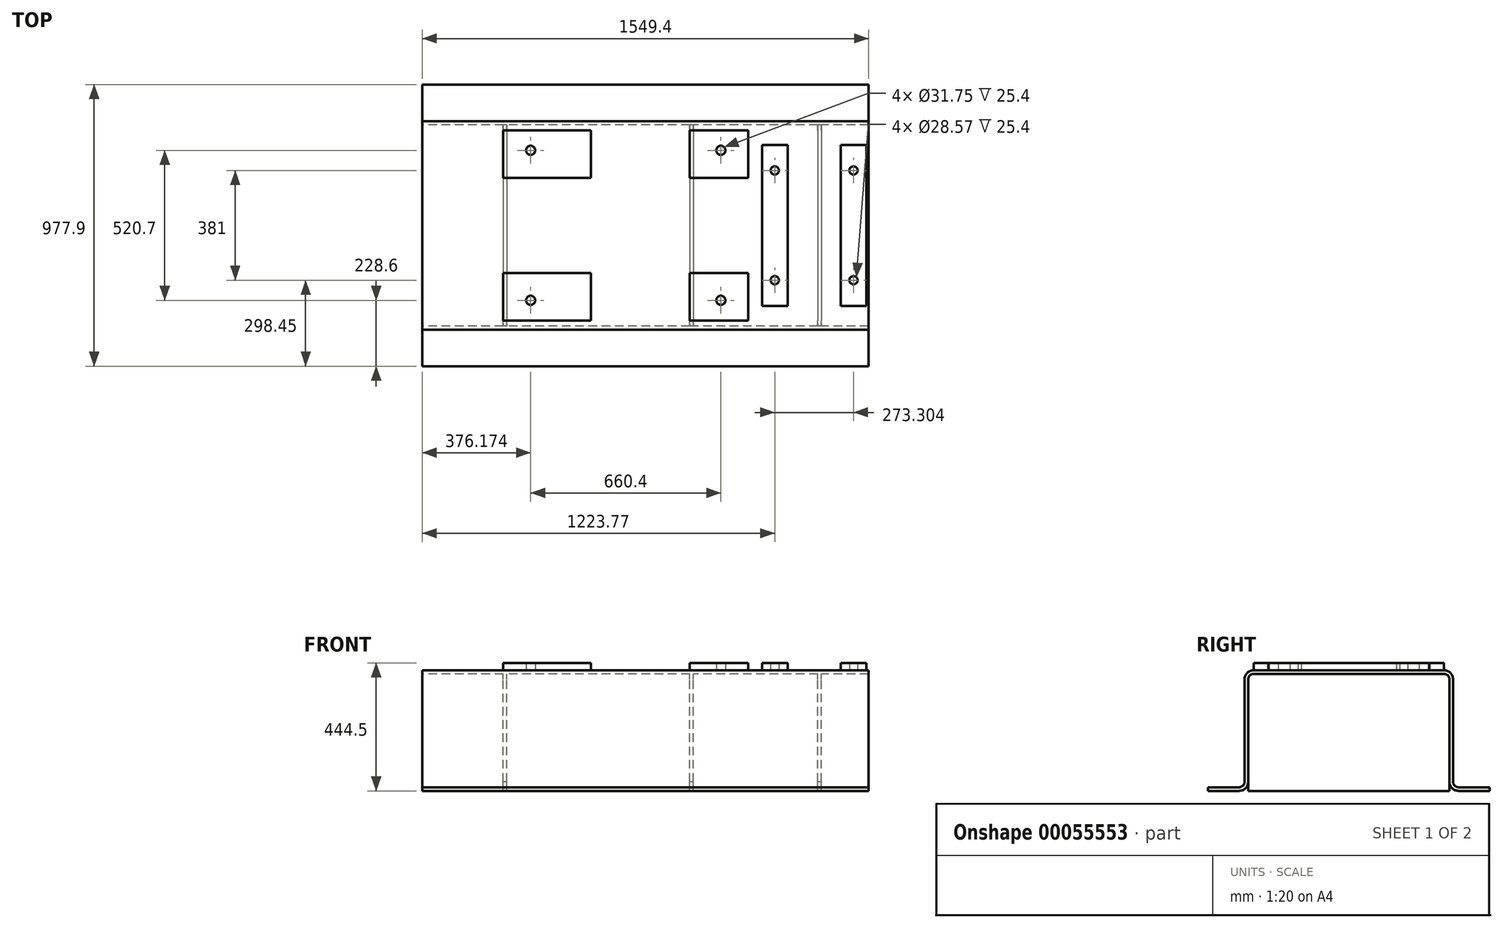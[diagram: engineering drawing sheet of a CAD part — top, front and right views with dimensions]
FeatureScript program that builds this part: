
annotation { "Feature Type Name" : "Feature", "Feature Type Description" : "" }
export const myFeature = defineFeature(function(context is Context, id is Id, definition is map)
    precondition{}
    {
        {
            var Q0;
            Q0=qCreatedBy(makeId("Right.planeOp"),FACE);
            var sketch = newSketch(context, id + "F0", { "sketchPlane" : qUnion([Q0])});
            skLineSegment(sketch, "E0", {"start": v(-488.95, 0) * mm, "end": v(488.95, 0) * mm, "construction": true});
            skLineSegment(sketch, "E1.0", {"start": v(-488.95, 419.1) * mm, "end": v(488.95, 419.1) * mm, "construction": true});
            skLineSegment(sketch, "E2", {"start": v(0, 0) * mm, "end": v(0, 550.43) * mm, "construction": true});
            skLineSegment(sketch, "E3.0", {"start": v(-361.95, 0) * mm, "end": v(-361.95, 550.43) * mm, "construction": true});
            skLineSegment(sketch, "E4.0", {"start": v(-488.95, 12.7) * mm, "end": v(488.95, 12.7) * mm, "construction": true});
            skLineSegment(sketch, "E5.0", {"start": v(-349.25, 0) * mm, "end": v(-349.25, 550.43) * mm, "construction": true});
            skLineSegment(sketch, "E6.0", {"start": v(-488.95, 406.4) * mm, "end": v(488.95, 406.4) * mm, "construction": true});
            skLineSegment(sketch, "E7", {"start": v(-488.95, 0) * mm, "end": v(-381, 0) * mm});
            skLineSegment(sketch, "E8", {"start": v(-349.25, 31.75) * mm, "end": v(-349.25, 387.35) * mm});
            skLineSegment(sketch, "E9", {"start": v(-330.2, 406.4) * mm, "end": v(0, 406.4) * mm});
            skLineSegment(sketch, "E10", {"start": v(0, 406.4) * mm, "end": v(0, 419.1) * mm});
            skLineSegment(sketch, "E11", {"start": v(0, 419.1) * mm, "end": v(-330.2, 419.1) * mm});
            skLineSegment(sketch, "E12", {"start": v(-361.95, 387.35) * mm, "end": v(-361.95, 31.75) * mm});
            skLineSegment(sketch, "E13", {"start": v(-381, 12.7) * mm, "end": v(-488.95, 12.7) * mm});
            skLineSegment(sketch, "E14", {"start": v(-488.95, 12.7) * mm, "end": v(-488.95, 0) * mm});
            skPoint(sketch, "E15.visualSharp", {"position": v(-349.25, 406.4) * mm});
            skArc(sketch, "E15.filletArc", {"start": v(-330.2, 406.4) * mm, "mid": v(-343.67, 400.82) * mm, "end": v(-349.25, 387.35) * mm});
            skPoint(sketch, "E16.visualSharp", {"position": v(-361.95, 12.7) * mm});
            skArc(sketch, "E16.filletArc", {"start": v(-381, 12.7) * mm, "mid": v(-367.53, 18.28) * mm, "end": v(-361.95, 31.75) * mm});
            skPoint(sketch, "E17.visualSharp", {"position": v(-349.25, 0) * mm});
            skArc(sketch, "E17.filletArc", {"start": v(-381, 0) * mm, "mid": v(-358.55, 9.3) * mm, "end": v(-349.25, 31.75) * mm});
            skPoint(sketch, "E18.visualSharp", {"position": v(-361.95, 419.1) * mm});
            skArc(sketch, "E18.filletArc", {"start": v(-330.2, 419.1) * mm, "mid": v(-352.65, 409.8) * mm, "end": v(-361.95, 387.35) * mm});
            skArc(sketch, "E19.MirrorCS", {"start": v(381, 12.7) * mm, "mid": v(367.53, 18.28) * mm, "end": v(361.95, 31.75) * mm});
            skLineSegment(sketch, "E20.MirrorCS", {"start": v(488.95, 12.7) * mm, "end": v(488.95, 0) * mm});
            skArc(sketch, "E21.MirrorCS", {"start": v(330.2, 406.4) * mm, "mid": v(343.67, 400.82) * mm, "end": v(349.25, 387.35) * mm});
            skArc(sketch, "E22.MirrorCS", {"start": v(381, 0) * mm, "mid": v(358.55, 9.3) * mm, "end": v(349.25, 31.75) * mm});
            skArc(sketch, "E23.MirrorCS", {"start": v(330.2, 419.1) * mm, "mid": v(352.65, 409.8) * mm, "end": v(361.95, 387.35) * mm});
            skPoint(sketch, "E24.MirrorP", {"position": v(361.95, 419.1) * mm});
            skLineSegment(sketch, "E25.MirrorCS", {"start": v(488.95, 0) * mm, "end": v(381, 0) * mm});
            skPoint(sketch, "E26.MirrorP", {"position": v(349.25, 0) * mm});
            skLineSegment(sketch, "E27.MirrorCS", {"start": v(330.2, 406.4) * mm, "end": v(0, 406.4) * mm});
            skLineSegment(sketch, "E28.MirrorCS", {"start": v(349.25, 31.75) * mm, "end": v(349.25, 387.35) * mm});
            skLineSegment(sketch, "E29.MirrorCS", {"start": v(381, 12.7) * mm, "end": v(488.95, 12.7) * mm});
            skLineSegment(sketch, "E30.MirrorCS", {"start": v(361.95, 387.35) * mm, "end": v(361.95, 31.75) * mm});
            skLineSegment(sketch, "E31.MirrorCS", {"start": v(0, 419.1) * mm, "end": v(330.2, 419.1) * mm});
            skPoint(sketch, "E32.MirrorP", {"position": v(349.25, 406.4) * mm});
            skPoint(sketch, "E33.MirrorP", {"position": v(361.95, 12.7) * mm});
            skSolve(sketch);
        }
        {
            var Q0;
            Q0 = qSketchRegion(id + "F0", true);
            extrude(context, id + "F1", {"entities" : qUnion([Q0]), "endBound" : BoundingType.SYMMETRIC, "depth" : 1549.4 * mm});
        }
        {
            var Q0;
            Q0=makeQuery(id+"F1.opExtrude","SWEPT_FACE",FACE,{"disambiguationData":[OSD([sQuery(id+"F0.wireOp",EDGE,"E11"),sQuery(id+"F0.wireOp",EDGE,"E31.MirrorCS")])]});
            var sketch = newSketch(context, id + "F2", { "sketchPlane" : qUnion([Q0])});
            skLineSegment(sketch, "E34.0", {"start": v(774.7, 330.2) * mm, "end": v(774.7, -330.2) * mm, "construction": true});
            skLineSegment(sketch, "E35.0", {"start": v(-1612.9, 330.2) * mm, "end": v(-1612.9, -330.2) * mm, "construction": true});
            skLineSegment(sketch, "E36.0", {"start": v(-1130.3, 330.2) * mm, "end": v(-1130.3, -330.2) * mm, "construction": true});
            skLineSegment(sketch, "E37.0", {"start": v(-68.33, 330.2) * mm, "end": v(-68.33, -330.2) * mm, "construction": true});
            skLineSegment(sketch, "E38.0", {"start": v(585.72, 330.2) * mm, "end": v(585.72, -330.2) * mm, "construction": true});
            skLineSegment(sketch, "E39", {"start": v(1112.44, 0) * mm, "end": v(-1758.43, 0) * mm, "construction": true});
            skLineSegment(sketch, "E40.0", {"start": v(153.92, 330.2) * mm, "end": v(153.92, -330.2) * mm, "construction": true});
            skLineSegment(sketch, "E41.0", {"start": v(357.12, 330.2) * mm, "end": v(357.12, -330.2) * mm, "construction": true});
            skLineSegment(sketch, "E42.0", {"start": v(-188.98, 330.2) * mm, "end": v(-188.98, -330.2) * mm, "construction": true});
            skLineSegment(sketch, "E43.0", {"start": v(-493.78, 330.2) * mm, "end": v(-493.78, -330.2) * mm, "construction": true});
            skLineSegment(sketch, "E44.0", {"start": v(1112.44, 165.1) * mm, "end": v(-1758.43, 165.1) * mm, "construction": true});
            skLineSegment(sketch, "E45.0", {"start": v(1112.44, 330.2) * mm, "end": v(-1758.43, 330.2) * mm, "construction": true});
            skLineSegment(sketch, "E46.bottom", {"start": v(-493.78, 330.2) * mm, "end": v(-188.98, 330.2) * mm});
            skLineSegment(sketch, "E46.top", {"start": v(-493.78, 165.1) * mm, "end": v(-188.98, 165.1) * mm});
            skLineSegment(sketch, "E46.left", {"start": v(-493.78, 330.2) * mm, "end": v(-493.78, 165.1) * mm});
            skLineSegment(sketch, "E46.right", {"start": v(-188.98, 330.2) * mm, "end": v(-188.98, 165.1) * mm});
            skLineSegment(sketch, "E47.bottom", {"start": v(153.92, 330.2) * mm, "end": v(357.12, 330.2) * mm});
            skLineSegment(sketch, "E47.top", {"start": v(153.92, 165.1) * mm, "end": v(357.12, 165.1) * mm});
            skLineSegment(sketch, "E47.left", {"start": v(153.92, 330.2) * mm, "end": v(153.92, 165.1) * mm});
            skLineSegment(sketch, "E47.right", {"start": v(357.12, 330.2) * mm, "end": v(357.12, 165.1) * mm});
            skLineSegment(sketch, "E48.0", {"start": v(-398.53, 330.2) * mm, "end": v(-398.53, -330.2) * mm, "construction": true});
            skLineSegment(sketch, "E49.0", {"start": v(261.87, 330.2) * mm, "end": v(261.87, -330.2) * mm, "construction": true});
            skLineSegment(sketch, "E50.0", {"start": v(1112.44, 260.35) * mm, "end": v(-1758.43, 260.35) * mm, "construction": true});
            skCircle(sketch, "E51", {"center": v(-398.53, 260.35) * mm, "radius": 15.88 * mm});
            skCircle(sketch, "E52", {"center": v(261.87, 260.35) * mm, "radius": 15.88 * mm});
            skLineSegment(sketch, "E53.MirrorCS", {"start": v(-493.78, -165.1) * mm, "end": v(-188.98, -165.1) * mm});
            skLineSegment(sketch, "E54.MirrorCS", {"start": v(-493.78, -330.2) * mm, "end": v(-188.98, -330.2) * mm});
            skLineSegment(sketch, "E55.MirrorCS", {"start": v(-493.78, -330.2) * mm, "end": v(-493.78, -165.1) * mm});
            skLineSegment(sketch, "E56.MirrorCS", {"start": v(-188.98, -330.2) * mm, "end": v(-188.98, -165.1) * mm});
            skLineSegment(sketch, "E57.MirrorCS", {"start": v(153.92, -330.2) * mm, "end": v(357.12, -330.2) * mm});
            skLineSegment(sketch, "E58.MirrorCS", {"start": v(153.92, -165.1) * mm, "end": v(357.12, -165.1) * mm});
            skCircle(sketch, "E59.MirrorC", {"center": v(-398.53, -260.35) * mm, "radius": 15.88 * mm});
            skLineSegment(sketch, "E60.MirrorCS", {"start": v(357.12, -330.2) * mm, "end": v(357.12, -165.1) * mm});
            skLineSegment(sketch, "E61.MirrorCS", {"start": v(153.92, -330.2) * mm, "end": v(153.92, -165.1) * mm});
            skCircle(sketch, "E62.MirrorC", {"center": v(261.87, -260.35) * mm, "radius": 15.88 * mm});
            skSolve(sketch);
        }
        {
            var Q0;
            Q0 = qSketchRegion(id + "F2", true);
            extrude(context, id + "F3", {"entities" : qUnion([Q0]), "operationType" : NewBodyOperationType.ADD, "depth" : 25.4 * mm});
        }
        {
            var Q0;
            Q0=makeQuery(id+"F1.opExtrude","SWEPT_FACE",FACE,{"disambiguationData":[OSD([sQuery(id+"F0.wireOp",EDGE,"E9"),sQuery(id+"F0.wireOp",EDGE,"E27.MirrorCS")])]});
            var sketch = newSketch(context, id + "F4", { "sketchPlane" : qUnion([Q0])});
            skLineSegment(sketch, "E63.0", {"start": v(585.72, -330.2) * mm, "end": v(585.72, 330.2) * mm, "construction": true});
            skLineSegment(sketch, "E64.0", {"start": v(1112.44, 0) * mm, "end": v(-1758.43, 0) * mm, "construction": true});
            skLineSegment(sketch, "E65.0", {"start": v(493.78, -330.2) * mm, "end": v(493.78, 330.2) * mm, "construction": true});
            skLineSegment(sketch, "E66.0", {"start": v(677.67, -330.2) * mm, "end": v(677.67, 330.2) * mm, "construction": true});
            skLineSegment(sketch, "E67.0", {"start": v(766.57, -330.2) * mm, "end": v(766.57, 330.2) * mm, "construction": true});
            skLineSegment(sketch, "E68.0", {"start": v(404.88, -330.2) * mm, "end": v(404.88, 330.2) * mm, "construction": true});
            skLineSegment(sketch, "E69.bottom", {"start": v(404.88, -279.4) * mm, "end": v(493.78, -279.4) * mm});
            skLineSegment(sketch, "E69.top", {"start": v(404.88, 279.4) * mm, "end": v(493.78, 279.4) * mm});
            skLineSegment(sketch, "E69.left", {"start": v(404.88, -279.4) * mm, "end": v(404.88, 279.4) * mm});
            skLineSegment(sketch, "E69.right", {"start": v(493.78, -279.4) * mm, "end": v(493.78, 279.4) * mm});
            skLineSegment(sketch, "E70.bottom", {"start": v(677.67, 279.4) * mm, "end": v(766.57, 279.4) * mm});
            skLineSegment(sketch, "E70.top", {"start": v(677.67, -279.4) * mm, "end": v(766.57, -279.4) * mm});
            skLineSegment(sketch, "E70.left", {"start": v(677.67, 279.4) * mm, "end": v(677.67, -279.4) * mm});
            skLineSegment(sketch, "E70.right", {"start": v(766.57, 279.4) * mm, "end": v(766.57, -279.4) * mm});
            skLineSegment(sketch, "E71.0", {"start": v(449.07, -330.2) * mm, "end": v(449.07, 330.2) * mm, "construction": true});
            skLineSegment(sketch, "E72.0", {"start": v(1112.44, -190.5) * mm, "end": v(-1758.43, -190.5) * mm, "construction": true});
            skCircle(sketch, "E73", {"center": v(449.07, -190.5) * mm, "radius": 14.29 * mm});
            skCircle(sketch, "E74.MirrorC", {"center": v(449.07, 190.5) * mm, "radius": 14.29 * mm});
            skCircle(sketch, "E75.MirrorC", {"center": v(722.38, -190.5) * mm, "radius": 14.29 * mm});
            skCircle(sketch, "E76.MirrorC", {"center": v(722.38, 190.5) * mm, "radius": 14.29 * mm});
            skSolve(sketch);
        }
        {
            var Q0;
            Q0 = qSketchRegion(id + "F4", true);
            var Q1;
            Q1=makeQuery(id+"F3.opExtrude","CAP_FACE",FACE,{"disambiguationData":[OSD([sQuery(id+"F2.wireOp",EDGE,"E60.MirrorCS"),sQuery(id+"F2.wireOp",EDGE,"E62.MirrorC"),sQuery(id+"F2.wireOp",EDGE,"E61.MirrorCS"),sQuery(id+"F2.wireOp",EDGE,"E58.MirrorCS"),sQuery(id+"F2.wireOp",EDGE,"E57.MirrorCS")])],"isStart":false});
            extrude(context, id + "F5", {"entities" : qUnion([Q0]), "operationType" : NewBodyOperationType.ADD, "endBound" : BoundingType.UP_TO_SURFACE, "oppositeDirection" : true, "endBoundEntityFace" : qUnion([Q1]), "depth" : 107.97 * mm});
        }
        {
            var Q0;
            {var subQ4=sQuery(id+"F0.wireOp",EDGE,"E27.MirrorCS");var subQ14=sQuery(id+"F0.wireOp",EDGE,"E15.filletArc");var subQ19=sQuery(id+"F0.wireOp",EDGE,"E9");Q0=makeQuery(id+"F5.boolean.opBoolean","SPLIT",FACE,{"disambiguationData":[TD([makeQuery(id+"F1.opExtrude","SWEPT_FACE",FACE,{"disambiguationData":[OSD([subQ14])]})])],"derivedFrom":makeQuery(id+"F1.opExtrude","SWEPT_FACE",FACE,{"disambiguationData":[OSD([subQ19,subQ4])]})});}
            var sketch = newSketch(context, id + "F6", { "sketchPlane" : qUnion([Q0])});
            skLineSegment(sketch, "E77.0", {"start": v(-68.33, -330.2) * mm, "end": v(-68.33, 330.2) * mm, "construction": true});
            skLineSegment(sketch, "E78.0", {"start": v(-481.08, -349.25) * mm, "end": v(-481.08, 349.25) * mm});
            skLineSegment(sketch, "E79.0", {"start": v(-493.78, -349.25) * mm, "end": v(-493.78, 349.25) * mm});
            skLineSegment(sketch, "E80.0", {"start": v(153.92, -349.25) * mm, "end": v(153.92, 349.25) * mm});
            skLineSegment(sketch, "E81.0", {"start": v(166.62, -349.25) * mm, "end": v(166.62, 349.25) * mm});
            skLineSegment(sketch, "E82.0", {"start": v(598.42, -349.25) * mm, "end": v(598.42, 349.25) * mm});
            skLineSegment(sketch, "E83.0", {"start": v(611.12, -349.25) * mm, "end": v(611.12, 349.25) * mm});
            skLineSegment(sketch, "E84.0", {"start": v(611.12, 349.25) * mm, "end": v(598.42, 349.25) * mm});
            skLineSegment(sketch, "E85.0", {"start": v(611.12, -349.25) * mm, "end": v(598.42, -349.25) * mm});
            skPoint(sketch, "E86.orphan", {"position": v(-774.7, 349.25) * mm});
            skLineSegment(sketch, "E87.trimOffspring", {"start": v(-481.08, 349.25) * mm, "end": v(-493.78, 349.25) * mm});
            skLineSegment(sketch, "E88.trimOffspring", {"start": v(166.62, 349.25) * mm, "end": v(153.92, 349.25) * mm});
            skPoint(sketch, "E89.orphan", {"position": v(774.7, 349.25) * mm});
            skPoint(sketch, "E90.orphan", {"position": v(774.7, -349.25) * mm});
            skLineSegment(sketch, "E91.trimOffspring", {"start": v(166.62, -349.25) * mm, "end": v(153.92, -349.25) * mm});
            skLineSegment(sketch, "E92.trimOffspring", {"start": v(-481.08, -349.25) * mm, "end": v(-493.78, -349.25) * mm});
            skPoint(sketch, "E93.orphan", {"position": v(-774.7, -349.25) * mm});
            skSolve(sketch);
        }
        {
            var Q0;
            Q0 = qSketchRegion(id + "F6", true);
            var Q1;
            Q1=makeQuery(id+"F1.opExtrude","SWEPT_FACE",FACE,{"disambiguationData":[OSD([sQuery(id+"F0.wireOp",EDGE,"E25.MirrorCS")])]});
            extrude(context, id + "F7", {"entities" : qUnion([Q0]), "operationType" : NewBodyOperationType.ADD, "endBound" : BoundingType.UP_TO_SURFACE, "endBoundEntityFace" : qUnion([Q1]), "depth" : 25.4 * mm});
        }
    });
